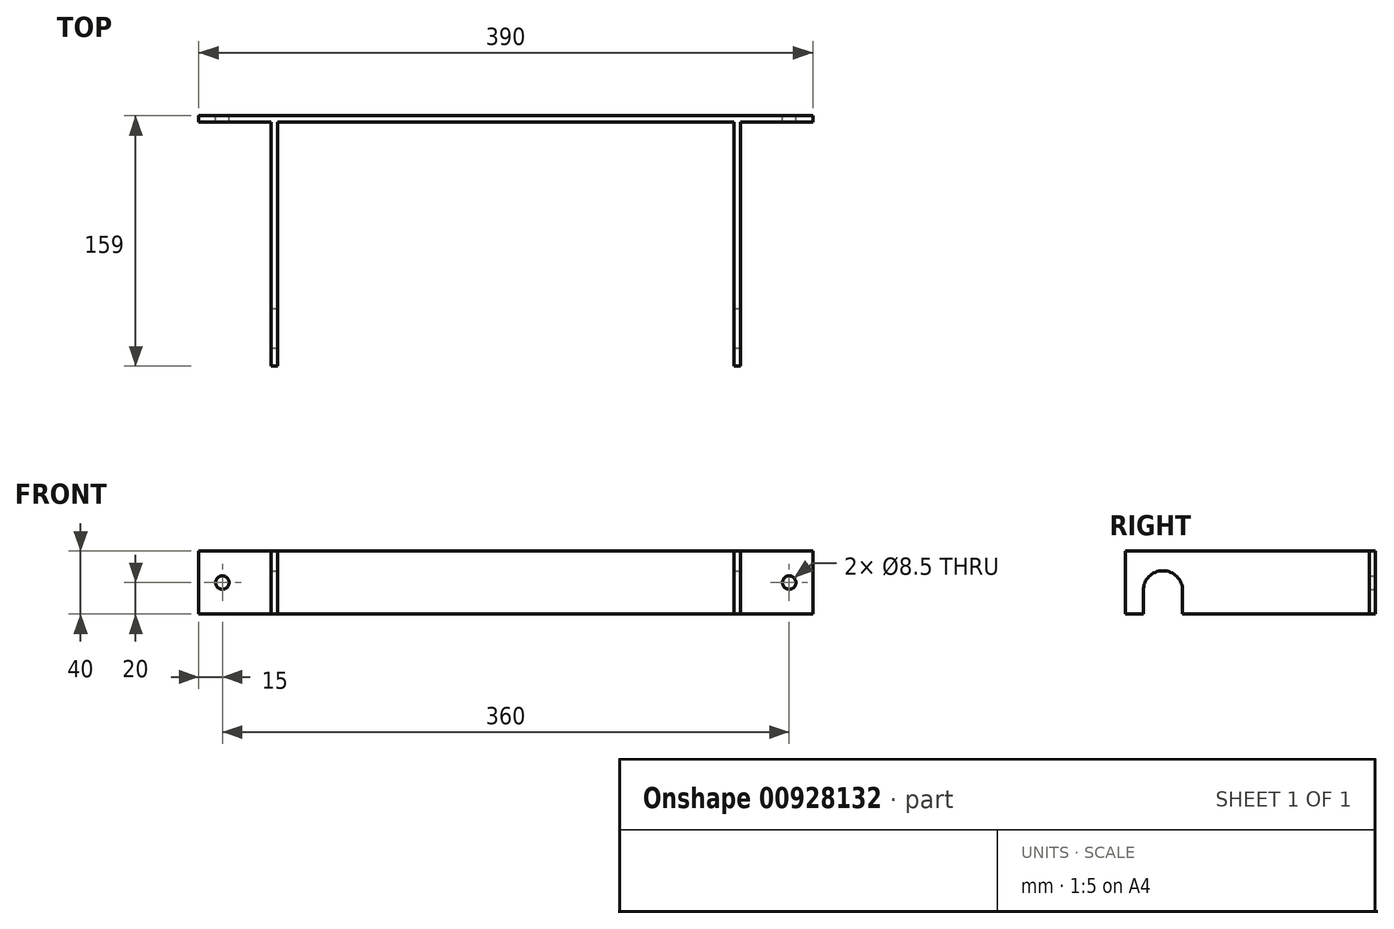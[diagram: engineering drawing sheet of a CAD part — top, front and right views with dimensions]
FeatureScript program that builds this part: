
annotation { "Feature Type Name" : "Feature", "Feature Type Description" : "" }
export const myFeature = defineFeature(function(context is Context, id is Id, definition is map)
    precondition{}
    {
        {
            var Q0;
            Q0=qCreatedBy(makeId("Front.planeOp"),FACE);
            var sketch = newSketch(context, id + "F0", { "sketchPlane" : qUnion([Q0])});
            skLineSegment(sketch, "E0.bottom", {"start": v(0, 0) * mm, "end": v(390, 0) * mm});
            skLineSegment(sketch, "E0.top", {"start": v(0, 40) * mm, "end": v(390, 40) * mm});
            skLineSegment(sketch, "E0.left", {"start": v(0, 0) * mm, "end": v(0, 40) * mm});
            skLineSegment(sketch, "E0.right", {"start": v(390, 0) * mm, "end": v(390, 40) * mm});
            skCircle(sketch, "E1", {"center": v(15, 20) * mm, "radius": 4.25 * mm});
            skCircle(sketch, "E2", {"center": v(375, 20) * mm, "radius": 4.25 * mm});
            skSolve(sketch);
        }
        {
            var Q0;
            Q0 = qSketchRegion(id + "F0", true);
            extrude(context, id + "F1", {"entities" : qUnion([Q0]), "depth" : 4 * mm, "offsetDistance" : 25 * mm});
        }
        {
            var Q0;
            Q0=makeQuery(id+"F1.opExtrude","CAP_FACE",FACE,{"disambiguationData":[OSD([sQuery(id+"F0.wireOp",EDGE,"E0.bottom"),sQuery(id+"F0.wireOp",EDGE,"E0.top"),sQuery(id+"F0.wireOp",EDGE,"E0.left"),sQuery(id+"F0.wireOp",EDGE,"E0.right"),sQuery(id+"F0.wireOp",EDGE,"E1"),sQuery(id+"F0.wireOp",EDGE,"E2")])],"isStart":false});
            var sketch = newSketch(context, id + "F2", { "sketchPlane" : qUnion([Q0])});
            skLineSegment(sketch, "E3.bottom", {"start": v(46, 40) * mm, "end": v(50, 40) * mm});
            skLineSegment(sketch, "E3.top", {"start": v(46, 0) * mm, "end": v(50, 0) * mm});
            skLineSegment(sketch, "E3.left", {"start": v(46, 40) * mm, "end": v(46, 0) * mm});
            skLineSegment(sketch, "E3.right", {"start": v(50, 40) * mm, "end": v(50, 0) * mm});
            skLineSegment(sketch, "E4.bottom", {"start": v(340, 40) * mm, "end": v(344, 40) * mm});
            skLineSegment(sketch, "E4.top", {"start": v(340, 0) * mm, "end": v(344, 0) * mm});
            skLineSegment(sketch, "E4.left", {"start": v(340, 40) * mm, "end": v(340, 0) * mm});
            skLineSegment(sketch, "E4.right", {"start": v(344, 40) * mm, "end": v(344, 0) * mm});
            skSolve(sketch);
        }
        {
            var Q0;
            Q0 = qSketchRegion(id + "F2", true);
            extrude(context, id + "F3", {"entities" : qUnion([Q0]), "operationType" : NewBodyOperationType.ADD, "depth" : 155 * mm, "offsetDistance" : 25 * mm});
        }
        {
            var Q0;
            Q0=makeQuery(id+"F3.opExtrude","SWEPT_FACE",FACE,{"disambiguationData":[OSD([sQuery(id+"F2.wireOp",EDGE,"E4.right")])]});
            var sketch = newSketch(context, id + "F4", { "sketchPlane" : qUnion([Q0])});
            skArc(sketch, "E5", {"start": v(-122.5, 15) * mm, "mid": v(-135, 27.5) * mm, "end": v(-147.5, 15) * mm});
            skLineSegment(sketch, "E6", {"start": v(-147.5, 15) * mm, "end": v(-147.5, 0) * mm});
            skLineSegment(sketch, "E7", {"start": v(-122.5, 15) * mm, "end": v(-122.5, 0) * mm});
            skLineSegment(sketch, "E8", {"start": v(-122.5, 0) * mm, "end": v(-147.5, 0) * mm});
            skSolve(sketch);
        }
        {
            var Q0;
            Q0=makeQuery(id+"F4.imprint","IMPRINT",FACE,{"disambiguationData":[TD([[makeQuery(id+"F4.imprint","IMPRINT",EDGE,{"derivedFrom":sQuery(id+"F4.wireOp",EDGE,"E5")}),1.0]])]});
            var Q1;
            Q1=makeQuery(id+"F3.opExtrude","SWEPT_FACE",FACE,{"disambiguationData":[OSD([sQuery(id+"F2.wireOp",EDGE,"E3.left")])]});
            extrude(context, id + "F5", {"entities" : qUnion([Q0]), "operationType" : NewBodyOperationType.REMOVE, "endBound" : BoundingType.UP_TO_SURFACE, "oppositeDirection" : true, "depth" : 25 * mm, "endBoundEntityFace" : qUnion([Q1]), "offsetDistance" : 25 * mm});
        }
    });
